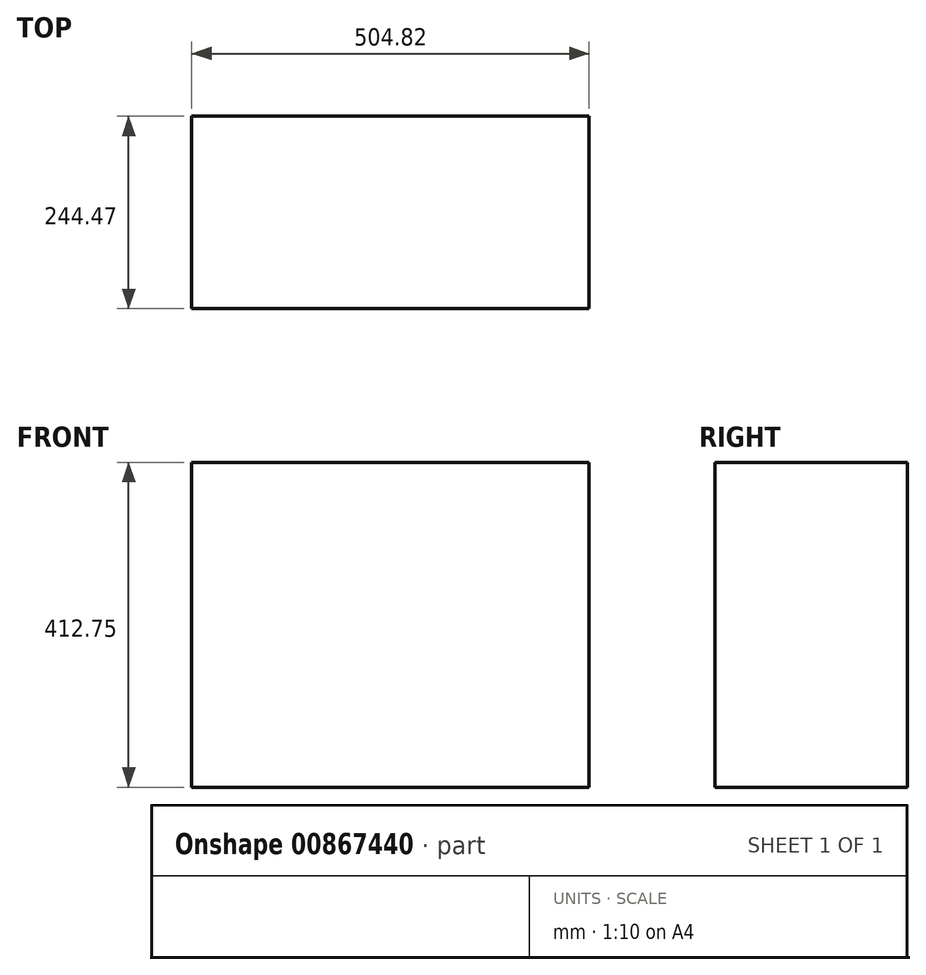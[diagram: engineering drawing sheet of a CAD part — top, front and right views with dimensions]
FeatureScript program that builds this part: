
annotation { "Feature Type Name" : "Feature", "Feature Type Description" : "" }
export const myFeature = defineFeature(function(context is Context, id is Id, definition is map)
    precondition{}
    {
        {
            var Q0;
            Q0=qCreatedBy(makeId("Front.planeOp"),FACE);
            var sketch = newSketch(context, id + "F0", { "sketchPlane" : qUnion([Q0])});
            skLineSegment(sketch, "E0.bottom", {"start": v(0, 0) * mm, "end": v(504.83, 0) * mm});
            skLineSegment(sketch, "E0.top", {"start": v(0, 412.75) * mm, "end": v(504.82, 412.75) * mm});
            skLineSegment(sketch, "E0.left", {"start": v(0, 0) * mm, "end": v(0, 412.75) * mm});
            skLineSegment(sketch, "E0.right", {"start": v(504.83, 0) * mm, "end": v(504.83, 412.75) * mm});
            skSolve(sketch);
        }
        {
            var Q0;
            Q0=qSketchRegion(id+"F0",true);
            extrude(context, id + "F1", {"entities" : qUnion([Q0]), "depth" : 244.47 * mm, "offsetDistance" : 25.4 * mm});
        }
    });
